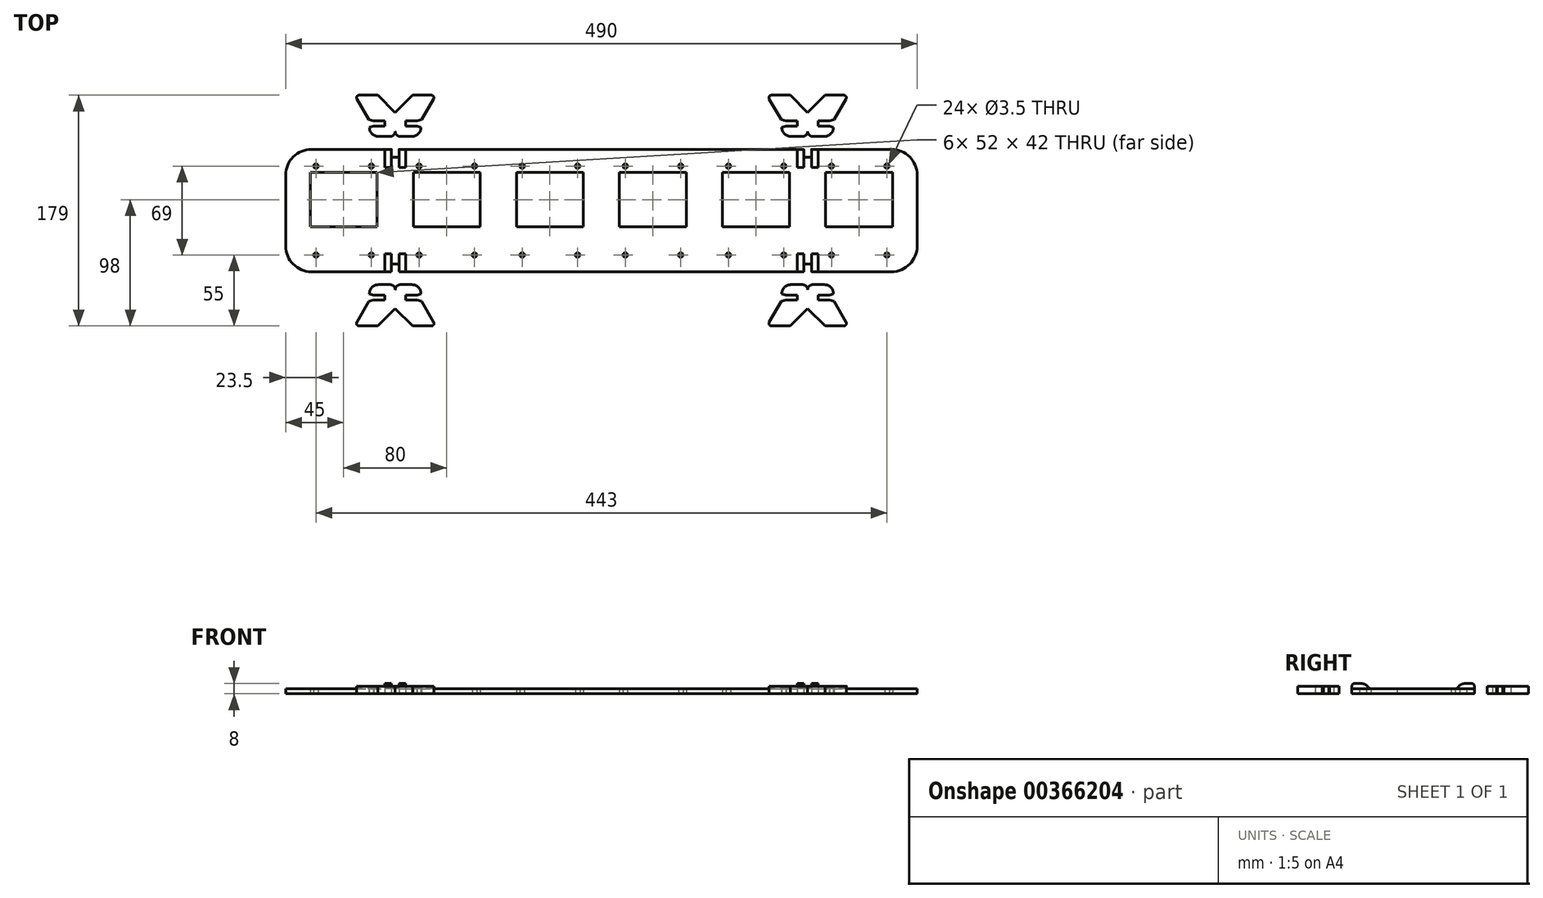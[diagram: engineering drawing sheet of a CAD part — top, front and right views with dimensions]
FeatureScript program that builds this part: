
annotation { "Feature Type Name" : "Feature", "Feature Type Description" : "" }
export const myFeature = defineFeature(function(context is Context, id is Id, definition is map)
    precondition{}
    {
        {
            var Q0;
            Q0=qCreatedBy(makeId("Top.planeOp"),FACE);
            var sketch = newSketch(context, id + "F0", { "sketchPlane" : qUnion([Q0])});
            skLineSegment(sketch, "E0.bottom", {"start": v(-245, -47.5) * mm, "end": v(245, -47.5) * mm});
            skLineSegment(sketch, "E0.top", {"start": v(-245, 47.5) * mm, "end": v(245, 47.5) * mm});
            skLineSegment(sketch, "E0.left", {"start": v(-245, -47.5) * mm, "end": v(-245, 47.5) * mm});
            skLineSegment(sketch, "E0.right", {"start": v(245, -47.5) * mm, "end": v(245, 47.5) * mm});
            skPoint(sketch, "E0.middle", {"position": v(0, 0) * mm});
            skLineSegment(sketch, "E1", {"start": v(-245, 0) * mm, "end": v(245, 0) * mm, "construction": true});
            skLineSegment(sketch, "E2.bottom", {"start": v(-175, -37.5) * mm, "end": v(-225, -37.5) * mm, "construction": true});
            skLineSegment(sketch, "E2.top", {"start": v(-175, 37.5) * mm, "end": v(-225, 37.5) * mm, "construction": true});
            skLineSegment(sketch, "E2.left", {"start": v(-175, -37.5) * mm, "end": v(-175, 37.5) * mm, "construction": true});
            skLineSegment(sketch, "E2.right", {"start": v(-225, -37.5) * mm, "end": v(-225, 37.5) * mm, "construction": true});
            skPoint(sketch, "E2.middle", {"position": v(-200, 0) * mm});
            skLineSegment(sketch, "E3.bottom", {"start": v(-95, -37.5) * mm, "end": v(-145, -37.5) * mm, "construction": true});
            skLineSegment(sketch, "E3.top", {"start": v(-95, 37.5) * mm, "end": v(-145, 37.5) * mm, "construction": true});
            skLineSegment(sketch, "E3.left", {"start": v(-95, -37.5) * mm, "end": v(-95, 37.5) * mm, "construction": true});
            skLineSegment(sketch, "E3.right", {"start": v(-145, -37.5) * mm, "end": v(-145, 37.5) * mm, "construction": true});
            skPoint(sketch, "E3.middle", {"position": v(-120, 0) * mm});
            skLineSegment(sketch, "E4.bottom", {"start": v(-15, -37.5) * mm, "end": v(-65, -37.5) * mm, "construction": true});
            skLineSegment(sketch, "E4.top", {"start": v(-15, 37.5) * mm, "end": v(-65, 37.5) * mm, "construction": true});
            skLineSegment(sketch, "E4.left", {"start": v(-15, -37.5) * mm, "end": v(-15, 37.5) * mm, "construction": true});
            skLineSegment(sketch, "E4.right", {"start": v(-65, -37.5) * mm, "end": v(-65, 37.5) * mm, "construction": true});
            skPoint(sketch, "E4.middle", {"position": v(-40, 0) * mm});
            skLineSegment(sketch, "E5.bottom", {"start": v(65, -37.5) * mm, "end": v(15, -37.5) * mm, "construction": true});
            skLineSegment(sketch, "E5.top", {"start": v(65, 37.5) * mm, "end": v(15, 37.5) * mm, "construction": true});
            skLineSegment(sketch, "E5.left", {"start": v(65, -37.5) * mm, "end": v(65, 37.5) * mm, "construction": true});
            skLineSegment(sketch, "E5.right", {"start": v(15, -37.5) * mm, "end": v(15, 37.5) * mm, "construction": true});
            skPoint(sketch, "E5.middle", {"position": v(40, 0) * mm});
            skLineSegment(sketch, "E6.bottom", {"start": v(145, -37.5) * mm, "end": v(95, -37.5) * mm, "construction": true});
            skLineSegment(sketch, "E6.top", {"start": v(145, 37.5) * mm, "end": v(95, 37.5) * mm, "construction": true});
            skLineSegment(sketch, "E6.left", {"start": v(145, -37.5) * mm, "end": v(145, 37.5) * mm, "construction": true});
            skLineSegment(sketch, "E6.right", {"start": v(95, -37.5) * mm, "end": v(95, 37.5) * mm, "construction": true});
            skPoint(sketch, "E6.middle", {"position": v(120, 0) * mm});
            skLineSegment(sketch, "E7.bottom", {"start": v(225, -37.5) * mm, "end": v(175, -37.5) * mm, "construction": true});
            skLineSegment(sketch, "E7.top", {"start": v(225, 37.5) * mm, "end": v(175, 37.5) * mm, "construction": true});
            skLineSegment(sketch, "E7.left", {"start": v(225, -37.5) * mm, "end": v(225, 37.5) * mm, "construction": true});
            skLineSegment(sketch, "E7.right", {"start": v(175, -37.5) * mm, "end": v(175, 37.5) * mm, "construction": true});
            skPoint(sketch, "E7.middle", {"position": v(200, 0) * mm});
            skLineSegment(sketch, "E8.bottom", {"start": v(305, -37.5) * mm, "end": v(255, -37.5) * mm, "construction": true});
            skLineSegment(sketch, "E8.top", {"start": v(305, 37.5) * mm, "end": v(255, 37.5) * mm, "construction": true});
            skLineSegment(sketch, "E8.left", {"start": v(305, -37.5) * mm, "end": v(305, 37.5) * mm, "construction": true});
            skLineSegment(sketch, "E8.right", {"start": v(255, -37.5) * mm, "end": v(255, 37.5) * mm, "construction": true});
            skPoint(sketch, "E8.middle", {"position": v(280, 0) * mm});
            skLineSegment(sketch, "E9.bottom", {"start": v(385, -37.5) * mm, "end": v(335, -37.5) * mm, "construction": true});
            skLineSegment(sketch, "E9.top", {"start": v(385, 37.5) * mm, "end": v(335, 37.5) * mm, "construction": true});
            skLineSegment(sketch, "E9.left", {"start": v(385, -37.5) * mm, "end": v(385, 37.5) * mm, "construction": true});
            skLineSegment(sketch, "E9.right", {"start": v(335, -37.5) * mm, "end": v(335, 37.5) * mm, "construction": true});
            skPoint(sketch, "E9.middle", {"position": v(360, 0) * mm});
            skLineSegment(sketch, "E10", {"start": v(-225, 0) * mm, "end": v(-245, 0) * mm, "construction": true});
            skLineSegment(sketch, "E11", {"start": v(335, 37.5) * mm, "end": v(325, 37.5) * mm});
            skLineSegment(sketch, "E12", {"start": v(315, 37.5) * mm, "end": v(325, 37.5) * mm});
            skLineSegment(sketch, "E13", {"start": v(315, 37.5) * mm, "end": v(305, 37.5) * mm, "construction": true});
            skLineSegment(sketch, "E14", {"start": v(255, 37.5) * mm, "end": v(245, 37.5) * mm, "construction": true});
            skLineSegment(sketch, "E15", {"start": v(245, 37.5) * mm, "end": v(235, 37.5) * mm, "construction": true});
            skLineSegment(sketch, "E16", {"start": v(235, 37.5) * mm, "end": v(225, 37.5) * mm, "construction": true});
            skLineSegment(sketch, "E17", {"start": v(155, 37.5) * mm, "end": v(145, 37.5) * mm, "construction": true});
            skLineSegment(sketch, "E18", {"start": v(95, 37.5) * mm, "end": v(85, 37.5) * mm, "construction": true});
            skLineSegment(sketch, "E19", {"start": v(85, 37.5) * mm, "end": v(75, 37.5) * mm, "construction": true});
            skLineSegment(sketch, "E20", {"start": v(75, 37.5) * mm, "end": v(65, 37.5) * mm, "construction": true});
            skLineSegment(sketch, "E21", {"start": v(15, 37.5) * mm, "end": v(5, 37.5) * mm, "construction": true});
            skLineSegment(sketch, "E22", {"start": v(5, 37.5) * mm, "end": v(-5, 37.5) * mm, "construction": true});
            skLineSegment(sketch, "E23", {"start": v(-5, 37.5) * mm, "end": v(-15, 37.5) * mm, "construction": true});
            skLineSegment(sketch, "E24", {"start": v(-65, 37.5) * mm, "end": v(-75, 37.5) * mm, "construction": true});
            skLineSegment(sketch, "E25", {"start": v(-75, 37.5) * mm, "end": v(-85, 37.5) * mm, "construction": true});
            skLineSegment(sketch, "E26", {"start": v(-85, 37.5) * mm, "end": v(-95, 37.5) * mm, "construction": true});
            skLineSegment(sketch, "E27", {"start": v(-145, 37.5) * mm, "end": v(-155, 37.5) * mm, "construction": true});
            skLineSegment(sketch, "E28", {"start": v(-155, 37.5) * mm, "end": v(-165, 37.5) * mm, "construction": true});
            skLineSegment(sketch, "E29", {"start": v(-165, 37.5) * mm, "end": v(-175, 37.5) * mm, "construction": true});
            skLineSegment(sketch, "E30", {"start": v(155, 37.5) * mm, "end": v(165, 37.5) * mm, "construction": true});
            skLineSegment(sketch, "E31", {"start": v(165, 37.5) * mm, "end": v(175, 37.5) * mm, "construction": true});
            skLineSegment(sketch, "E32", {"start": v(385, 37.5) * mm, "end": v(395, 37.5) * mm, "construction": true});
            skLineSegment(sketch, "E33.bottom", {"start": v(465, 37.5) * mm, "end": v(415, 37.5) * mm, "construction": true});
            skLineSegment(sketch, "E33.top", {"start": v(465, -37.5) * mm, "end": v(415, -37.5) * mm, "construction": true});
            skLineSegment(sketch, "E33.left", {"start": v(465, 37.5) * mm, "end": v(465, -37.5) * mm, "construction": true});
            skLineSegment(sketch, "E33.right", {"start": v(415, 37.5) * mm, "end": v(415, -37.5) * mm, "construction": true});
            skPoint(sketch, "E33.middle", {"position": v(440, 0) * mm});
            skLineSegment(sketch, "E34", {"start": v(395, 37.5) * mm, "end": v(405, 37.5) * mm, "construction": true});
            skLineSegment(sketch, "E35", {"start": v(405, 37.5) * mm, "end": v(415, 37.5) * mm, "construction": true});
            skLineSegment(sketch, "E36", {"start": v(465, 37.5) * mm, "end": v(475, 37.5) * mm, "construction": true});
            skLineSegment(sketch, "E37", {"start": v(475, 37.5) * mm, "end": v(485, 37.5) * mm, "construction": true});
            skLineSegment(sketch, "E38", {"start": v(485, 37.5) * mm, "end": v(495, 37.5) * mm, "construction": true});
            skLineSegment(sketch, "E39.bottom", {"start": v(495, 37.5) * mm, "end": v(545, 37.5) * mm, "construction": true});
            skLineSegment(sketch, "E39.top", {"start": v(495, -37.5) * mm, "end": v(545, -37.5) * mm, "construction": true});
            skLineSegment(sketch, "E39.left", {"start": v(495, 37.5) * mm, "end": v(495, -37.5) * mm, "construction": true});
            skLineSegment(sketch, "E39.right", {"start": v(545, 37.5) * mm, "end": v(545, -37.5) * mm, "construction": true});
            skPoint(sketch, "E39.middle", {"position": v(520, 0) * mm});
            skLineSegment(sketch, "E40.bottom", {"start": v(-178.5, -34.5) * mm, "end": v(-221.5, -34.5) * mm, "construction": true});
            skLineSegment(sketch, "E40.top", {"start": v(-178.5, 34.5) * mm, "end": v(-221.5, 34.5) * mm, "construction": true});
            skLineSegment(sketch, "E40.left", {"start": v(-178.5, -34.5) * mm, "end": v(-178.5, 34.5) * mm, "construction": true});
            skLineSegment(sketch, "E40.right", {"start": v(-221.5, -34.5) * mm, "end": v(-221.5, 34.5) * mm, "construction": true});
            skCircle(sketch, "E41", {"center": v(-178.5, 34.5) * mm, "radius": 1.75 * mm});
            skCircle(sketch, "E42", {"center": v(-221.5, 34.5) * mm, "radius": 1.75 * mm});
            skCircle(sketch, "E43", {"center": v(-221.5, -34.5) * mm, "radius": 1.75 * mm});
            skCircle(sketch, "E44", {"center": v(-178.5, -34.5) * mm, "radius": 1.75 * mm});
            skLineSegment(sketch, "E45.bottom", {"start": v(-174, -12.5) * mm, "end": v(-226, -12.5) * mm});
            skLineSegment(sketch, "E45.top", {"start": v(-174, 29.5) * mm, "end": v(-226, 29.5) * mm});
            skLineSegment(sketch, "E45.left", {"start": v(-174, -12.5) * mm, "end": v(-174, 29.5) * mm});
            skLineSegment(sketch, "E45.right", {"start": v(-226, -12.5) * mm, "end": v(-226, 29.5) * mm});
            skPoint(sketch, "E45.middle", {"position": v(-200, 8.5) * mm});
            skLineSegment(sketch, "E46.bottom", {"start": v(-98.5, -34.5) * mm, "end": v(-141.5, -34.5) * mm, "construction": true});
            skLineSegment(sketch, "E46.top", {"start": v(-98.5, 34.5) * mm, "end": v(-141.5, 34.5) * mm, "construction": true});
            skLineSegment(sketch, "E46.left", {"start": v(-98.5, -34.5) * mm, "end": v(-98.5, 34.5) * mm, "construction": true});
            skLineSegment(sketch, "E46.right", {"start": v(-141.5, -34.5) * mm, "end": v(-141.5, 34.5) * mm, "construction": true});
            skCircle(sketch, "E47", {"center": v(-98.5, 34.5) * mm, "radius": 1.75 * mm});
            skCircle(sketch, "E48", {"center": v(-141.5, 34.5) * mm, "radius": 1.75 * mm});
            skCircle(sketch, "E49", {"center": v(-141.5, -34.5) * mm, "radius": 1.75 * mm});
            skCircle(sketch, "E50", {"center": v(-98.5, -34.5) * mm, "radius": 1.75 * mm});
            skLineSegment(sketch, "E51.bottom", {"start": v(-94, -12.5) * mm, "end": v(-146, -12.5) * mm});
            skLineSegment(sketch, "E51.top", {"start": v(-94, 29.5) * mm, "end": v(-146, 29.5) * mm});
            skLineSegment(sketch, "E51.left", {"start": v(-94, -12.5) * mm, "end": v(-94, 29.5) * mm});
            skLineSegment(sketch, "E51.right", {"start": v(-146, -12.5) * mm, "end": v(-146, 29.5) * mm});
            skPoint(sketch, "E51.middle", {"position": v(-120, 8.5) * mm});
            skLineSegment(sketch, "E52.bottom", {"start": v(-18.5, -34.5) * mm, "end": v(-61.5, -34.5) * mm, "construction": true});
            skLineSegment(sketch, "E52.top", {"start": v(-18.5, 34.5) * mm, "end": v(-61.5, 34.5) * mm, "construction": true});
            skLineSegment(sketch, "E52.left", {"start": v(-18.5, -34.5) * mm, "end": v(-18.5, 34.5) * mm, "construction": true});
            skLineSegment(sketch, "E52.right", {"start": v(-61.5, -34.5) * mm, "end": v(-61.5, 34.5) * mm, "construction": true});
            skCircle(sketch, "E53", {"center": v(-18.5, 34.5) * mm, "radius": 1.75 * mm});
            skCircle(sketch, "E54", {"center": v(-61.5, 34.5) * mm, "radius": 1.75 * mm});
            skCircle(sketch, "E55", {"center": v(-61.5, -34.5) * mm, "radius": 1.75 * mm});
            skCircle(sketch, "E56", {"center": v(-18.5, -34.5) * mm, "radius": 1.75 * mm});
            skLineSegment(sketch, "E57.bottom", {"start": v(-14, -12.5) * mm, "end": v(-66, -12.5) * mm});
            skLineSegment(sketch, "E57.top", {"start": v(-14, 29.5) * mm, "end": v(-66, 29.5) * mm});
            skLineSegment(sketch, "E57.left", {"start": v(-14, -12.5) * mm, "end": v(-14, 29.5) * mm});
            skLineSegment(sketch, "E57.right", {"start": v(-66, -12.5) * mm, "end": v(-66, 29.5) * mm});
            skPoint(sketch, "E57.middle", {"position": v(-40, 8.5) * mm});
            skLineSegment(sketch, "E58.bottom", {"start": v(61.5, -34.5) * mm, "end": v(18.5, -34.5) * mm, "construction": true});
            skLineSegment(sketch, "E58.top", {"start": v(61.5, 34.5) * mm, "end": v(18.5, 34.5) * mm, "construction": true});
            skLineSegment(sketch, "E58.left", {"start": v(61.5, -34.5) * mm, "end": v(61.5, 34.5) * mm, "construction": true});
            skLineSegment(sketch, "E58.right", {"start": v(18.5, -34.5) * mm, "end": v(18.5, 34.5) * mm, "construction": true});
            skCircle(sketch, "E59", {"center": v(61.5, 34.5) * mm, "radius": 1.75 * mm});
            skCircle(sketch, "E60", {"center": v(18.5, 34.5) * mm, "radius": 1.75 * mm});
            skCircle(sketch, "E61", {"center": v(18.5, -34.5) * mm, "radius": 1.75 * mm});
            skCircle(sketch, "E62", {"center": v(61.5, -34.5) * mm, "radius": 1.75 * mm});
            skLineSegment(sketch, "E63.bottom", {"start": v(66, -12.5) * mm, "end": v(14, -12.5) * mm});
            skLineSegment(sketch, "E63.top", {"start": v(66, 29.5) * mm, "end": v(14, 29.5) * mm});
            skLineSegment(sketch, "E63.left", {"start": v(66, -12.5) * mm, "end": v(66, 29.5) * mm});
            skLineSegment(sketch, "E63.right", {"start": v(14, -12.5) * mm, "end": v(14, 29.5) * mm});
            skPoint(sketch, "E63.middle", {"position": v(40, 8.5) * mm});
            skLineSegment(sketch, "E64.bottom", {"start": v(141.5, -34.5) * mm, "end": v(98.5, -34.5) * mm, "construction": true});
            skLineSegment(sketch, "E64.top", {"start": v(141.5, 34.5) * mm, "end": v(98.5, 34.5) * mm, "construction": true});
            skLineSegment(sketch, "E64.left", {"start": v(141.5, -34.5) * mm, "end": v(141.5, 34.5) * mm, "construction": true});
            skLineSegment(sketch, "E64.right", {"start": v(98.5, -34.5) * mm, "end": v(98.5, 34.5) * mm, "construction": true});
            skCircle(sketch, "E65", {"center": v(141.5, 34.5) * mm, "radius": 1.75 * mm});
            skCircle(sketch, "E66", {"center": v(98.5, 34.5) * mm, "radius": 1.75 * mm});
            skCircle(sketch, "E67", {"center": v(98.5, -34.5) * mm, "radius": 1.75 * mm});
            skCircle(sketch, "E68", {"center": v(141.5, -34.5) * mm, "radius": 1.75 * mm});
            skLineSegment(sketch, "E69.bottom", {"start": v(146, -12.5) * mm, "end": v(94, -12.5) * mm});
            skLineSegment(sketch, "E69.top", {"start": v(146, 29.5) * mm, "end": v(94, 29.5) * mm});
            skLineSegment(sketch, "E69.left", {"start": v(146, -12.5) * mm, "end": v(146, 29.5) * mm});
            skLineSegment(sketch, "E69.right", {"start": v(94, -12.5) * mm, "end": v(94, 29.5) * mm});
            skPoint(sketch, "E69.middle", {"position": v(120, 8.5) * mm});
            skLineSegment(sketch, "E70.bottom", {"start": v(221.5, -34.5) * mm, "end": v(178.5, -34.5) * mm, "construction": true});
            skLineSegment(sketch, "E70.top", {"start": v(221.5, 34.5) * mm, "end": v(178.5, 34.5) * mm, "construction": true});
            skLineSegment(sketch, "E70.left", {"start": v(221.5, -34.5) * mm, "end": v(221.5, 34.5) * mm, "construction": true});
            skLineSegment(sketch, "E70.right", {"start": v(178.5, -34.5) * mm, "end": v(178.5, 34.5) * mm, "construction": true});
            skCircle(sketch, "E71", {"center": v(221.5, 34.5) * mm, "radius": 1.75 * mm});
            skCircle(sketch, "E72", {"center": v(178.5, 34.5) * mm, "radius": 1.75 * mm});
            skCircle(sketch, "E73", {"center": v(178.5, -34.5) * mm, "radius": 1.75 * mm});
            skCircle(sketch, "E74", {"center": v(221.5, -34.5) * mm, "radius": 1.75 * mm});
            skLineSegment(sketch, "E75.bottom", {"start": v(226, -12.5) * mm, "end": v(174, -12.5) * mm});
            skLineSegment(sketch, "E75.top", {"start": v(226, 29.5) * mm, "end": v(174, 29.5) * mm});
            skLineSegment(sketch, "E75.left", {"start": v(226, -12.5) * mm, "end": v(226, 29.5) * mm});
            skLineSegment(sketch, "E75.right", {"start": v(174, -12.5) * mm, "end": v(174, 29.5) * mm});
            skPoint(sketch, "E75.middle", {"position": v(200, 8.5) * mm});
            skLineSegment(sketch, "E76.bottom", {"start": v(301.5, -34.5) * mm, "end": v(258.5, -34.5) * mm, "construction": true});
            skLineSegment(sketch, "E76.top", {"start": v(301.5, 34.5) * mm, "end": v(258.5, 34.5) * mm, "construction": true});
            skLineSegment(sketch, "E76.left", {"start": v(301.5, -34.5) * mm, "end": v(301.5, 34.5) * mm, "construction": true});
            skLineSegment(sketch, "E76.right", {"start": v(258.5, -34.5) * mm, "end": v(258.5, 34.5) * mm, "construction": true});
            skCircle(sketch, "E77", {"center": v(301.5, 34.5) * mm, "radius": 1.75 * mm});
            skCircle(sketch, "E78", {"center": v(258.5, 34.5) * mm, "radius": 1.75 * mm});
            skCircle(sketch, "E79", {"center": v(258.5, -34.5) * mm, "radius": 1.75 * mm});
            skCircle(sketch, "E80", {"center": v(301.5, -34.5) * mm, "radius": 1.75 * mm});
            skLineSegment(sketch, "E81.bottom", {"start": v(306, -12.5) * mm, "end": v(254, -12.5) * mm});
            skLineSegment(sketch, "E81.top", {"start": v(306, 29.5) * mm, "end": v(254, 29.5) * mm});
            skLineSegment(sketch, "E81.left", {"start": v(306, -12.5) * mm, "end": v(306, 29.5) * mm});
            skLineSegment(sketch, "E81.right", {"start": v(254, -12.5) * mm, "end": v(254, 29.5) * mm});
            skPoint(sketch, "E81.middle", {"position": v(280, 8.5) * mm});
            skLineSegment(sketch, "E82.bottom", {"start": v(381.5, -34.5) * mm, "end": v(338.5, -34.5) * mm, "construction": true});
            skLineSegment(sketch, "E82.top", {"start": v(381.5, 34.5) * mm, "end": v(338.5, 34.5) * mm, "construction": true});
            skLineSegment(sketch, "E82.left", {"start": v(381.5, -34.5) * mm, "end": v(381.5, 34.5) * mm, "construction": true});
            skLineSegment(sketch, "E82.right", {"start": v(338.5, -34.5) * mm, "end": v(338.5, 34.5) * mm, "construction": true});
            skCircle(sketch, "E83", {"center": v(381.5, 34.5) * mm, "radius": 1.75 * mm});
            skCircle(sketch, "E84", {"center": v(338.5, 34.5) * mm, "radius": 1.75 * mm});
            skCircle(sketch, "E85", {"center": v(338.5, -34.5) * mm, "radius": 1.75 * mm});
            skCircle(sketch, "E86", {"center": v(381.5, -34.5) * mm, "radius": 1.75 * mm});
            skLineSegment(sketch, "E87.bottom", {"start": v(386, -12.5) * mm, "end": v(334, -12.5) * mm});
            skLineSegment(sketch, "E87.top", {"start": v(386, 29.5) * mm, "end": v(334, 29.5) * mm});
            skLineSegment(sketch, "E87.left", {"start": v(386, -12.5) * mm, "end": v(386, 29.5) * mm});
            skLineSegment(sketch, "E87.right", {"start": v(334, -12.5) * mm, "end": v(334, 29.5) * mm});
            skPoint(sketch, "E87.middle", {"position": v(360, 8.5) * mm});
            skLineSegment(sketch, "E88.bottom", {"start": v(461.5, -34.5) * mm, "end": v(418.5, -34.5) * mm, "construction": true});
            skLineSegment(sketch, "E88.top", {"start": v(461.5, 34.5) * mm, "end": v(418.5, 34.5) * mm, "construction": true});
            skLineSegment(sketch, "E88.left", {"start": v(461.5, -34.5) * mm, "end": v(461.5, 34.5) * mm, "construction": true});
            skLineSegment(sketch, "E88.right", {"start": v(418.5, -34.5) * mm, "end": v(418.5, 34.5) * mm, "construction": true});
            skCircle(sketch, "E89", {"center": v(461.5, 34.5) * mm, "radius": 1.75 * mm});
            skCircle(sketch, "E90", {"center": v(418.5, 34.5) * mm, "radius": 1.75 * mm});
            skCircle(sketch, "E91", {"center": v(418.5, -34.5) * mm, "radius": 1.75 * mm});
            skCircle(sketch, "E92", {"center": v(461.5, -34.5) * mm, "radius": 1.75 * mm});
            skLineSegment(sketch, "E93.bottom", {"start": v(466, -12.5) * mm, "end": v(414, -12.5) * mm});
            skLineSegment(sketch, "E93.top", {"start": v(466, 29.5) * mm, "end": v(414, 29.5) * mm});
            skLineSegment(sketch, "E93.left", {"start": v(466, -12.5) * mm, "end": v(466, 29.5) * mm});
            skLineSegment(sketch, "E93.right", {"start": v(414, -12.5) * mm, "end": v(414, 29.5) * mm});
            skPoint(sketch, "E93.middle", {"position": v(440, 8.5) * mm});
            skLineSegment(sketch, "E94.bottom", {"start": v(541.5, -34.5) * mm, "end": v(498.5, -34.5) * mm, "construction": true});
            skLineSegment(sketch, "E94.top", {"start": v(541.5, 34.5) * mm, "end": v(498.5, 34.5) * mm, "construction": true});
            skLineSegment(sketch, "E94.left", {"start": v(541.5, -34.5) * mm, "end": v(541.5, 34.5) * mm, "construction": true});
            skLineSegment(sketch, "E94.right", {"start": v(498.5, -34.5) * mm, "end": v(498.5, 34.5) * mm, "construction": true});
            skCircle(sketch, "E95", {"center": v(541.5, 34.5) * mm, "radius": 1.75 * mm});
            skCircle(sketch, "E96", {"center": v(498.5, 34.5) * mm, "radius": 1.75 * mm});
            skCircle(sketch, "E97", {"center": v(498.5, -34.5) * mm, "radius": 1.75 * mm});
            skCircle(sketch, "E98", {"center": v(541.5, -34.5) * mm, "radius": 1.75 * mm});
            skLineSegment(sketch, "E99.bottom", {"start": v(546, -12.5) * mm, "end": v(494, -12.5) * mm});
            skLineSegment(sketch, "E99.top", {"start": v(546, 29.5) * mm, "end": v(494, 29.5) * mm});
            skLineSegment(sketch, "E99.left", {"start": v(546, -12.5) * mm, "end": v(546, 29.5) * mm});
            skLineSegment(sketch, "E99.right", {"start": v(494, -12.5) * mm, "end": v(494, 29.5) * mm});
            skPoint(sketch, "E99.middle", {"position": v(520, 8.5) * mm});
            skLineSegment(sketch, "E100", {"start": v(545, 37.5) * mm, "end": v(555, 37.5) * mm, "construction": true});
            skLineSegment(sketch, "E101.bottom", {"start": v(-157, -47.5) * mm, "end": v(-163, -47.5) * mm});
            skLineSegment(sketch, "E101.top", {"start": v(-157, -41.5) * mm, "end": v(-163, -41.5) * mm});
            skLineSegment(sketch, "E101.left", {"start": v(-157, -47.5) * mm, "end": v(-157, -41.5) * mm});
            skLineSegment(sketch, "E101.right", {"start": v(-163, -47.5) * mm, "end": v(-163, -41.5) * mm});
            skPoint(sketch, "E101.middle", {"position": v(-160, -44.5) * mm});
            skLineSegment(sketch, "E102.bottom", {"start": v(163, -41.5) * mm, "end": v(157, -41.5) * mm});
            skLineSegment(sketch, "E102.top", {"start": v(163, -47.5) * mm, "end": v(157, -47.5) * mm});
            skLineSegment(sketch, "E102.left", {"start": v(163, -41.5) * mm, "end": v(163, -47.5) * mm});
            skLineSegment(sketch, "E102.right", {"start": v(157, -41.5) * mm, "end": v(157, -47.5) * mm});
            skPoint(sketch, "E102.middle", {"position": v(160, -44.5) * mm});
            skLineSegment(sketch, "E103.bottom", {"start": v(-157, 47.5) * mm, "end": v(-163, 47.5) * mm});
            skLineSegment(sketch, "E103.top", {"start": v(-157, 41.5) * mm, "end": v(-163, 41.5) * mm});
            skLineSegment(sketch, "E103.left", {"start": v(-157, 47.5) * mm, "end": v(-157, 41.5) * mm});
            skLineSegment(sketch, "E103.right", {"start": v(-163, 47.5) * mm, "end": v(-163, 41.5) * mm});
            skPoint(sketch, "E103.middle", {"position": v(-160, 44.5) * mm});
            skLineSegment(sketch, "E104.bottom", {"start": v(163, 47.5) * mm, "end": v(157, 47.5) * mm});
            skLineSegment(sketch, "E104.top", {"start": v(163, 41.5) * mm, "end": v(157, 41.5) * mm});
            skLineSegment(sketch, "E104.left", {"start": v(163, 47.5) * mm, "end": v(163, 41.5) * mm});
            skLineSegment(sketch, "E104.right", {"start": v(157, 47.5) * mm, "end": v(157, 41.5) * mm});
            skPoint(sketch, "E104.middle", {"position": v(160, 44.5) * mm});
            skSolve(sketch);
        }
        {
            var Q0;
            Q0=makeQuery(id+"F0.imprint","IMPRINT",FACE,{"disambiguationData":[TD([[makeQuery(id+"F0.imprint","IMPRINT",EDGE,{"derivedFrom":sQuery(id+"F0.wireOp",EDGE,"E0.bottom")}),1.0]])]});
            extrude(context, id + "F1", {"entities" : qUnion([Q0]), "depth" : 4 * mm});
        }
        {
            var Q0;
            Q0=makeQuery(id+"F1.opExtrude","SWEPT_EDGE",EDGE,{"disambiguationData":[OSD([sQuery(id+"F0.wireOp",EDGE,"E0.bottom"),sQuery(id+"F0.wireOp",EDGE,"E0.left")])]});
            var Q1;
            Q1=makeQuery(id+"F1.opExtrude","SWEPT_EDGE",EDGE,{"disambiguationData":[OSD([sQuery(id+"F0.wireOp",EDGE,"E0.top"),sQuery(id+"F0.wireOp",EDGE,"E0.left")])]});
            var Q2;
            Q2=makeQuery(id+"F1.opExtrude","SWEPT_EDGE",EDGE,{"disambiguationData":[OSD([sQuery(id+"F0.wireOp",EDGE,"E0.top"),sQuery(id+"F0.wireOp",EDGE,"E0.right")])]});
            var Q3;
            Q3=makeQuery(id+"F1.opExtrude","SWEPT_EDGE",EDGE,{"disambiguationData":[OSD([sQuery(id+"F0.wireOp",EDGE,"E0.bottom"),sQuery(id+"F0.wireOp",EDGE,"E0.right")])]});
            fillet(context, id + "F2", {"entities" : qUnion([Q0, Q1, Q2, Q3]), "radius" : 20 * mm, "tangentPropagation" : true, "allowEdgeOverflow" : false});
        }
        {
            var Q0;
            Q0=qCreatedBy(makeId("Top.planeOp"),FACE);
            var sketch = newSketch(context, id + "F3", { "sketchPlane" : qUnion([Q0])});
            skLineSegment(sketch, "E105.bottom", {"start": v(-152, -65.5) * mm, "end": v(-140, -65.5) * mm});
            skLineSegment(sketch, "E105.top", {"start": v(-152, -69.5) * mm, "end": v(-140, -69.5) * mm});
            skLineSegment(sketch, "E105.left", {"start": v(-152, -65.5) * mm, "end": v(-152, -69.5) * mm});
            skLineSegment(sketch, "E105.right", {"start": v(-140, -65.5) * mm, "end": v(-140, -69.5) * mm, "construction": true});
            skLineSegment(sketch, "E106", {"start": v(-160, -61.5) * mm, "end": v(-160, -75.95) * mm});
            skLineSegment(sketch, "E107", {"start": v(-160, -75.95) * mm, "end": v(-146.45, -89.5) * mm});
            skLineSegment(sketch, "E108", {"start": v(-146.45, -89.5) * mm, "end": v(-131.92, -89.5) * mm});
            skLineSegment(sketch, "E109", {"start": v(-130.19, -86.5) * mm, "end": v(-140, -69.5) * mm});
            skLineSegment(sketch, "E110", {"start": v(-156, -57.5) * mm, "end": v(-147, -57.5) * mm});
            skLineSegment(sketch, "E111", {"start": v(-140, -65.5) * mm, "end": v(-140, -64.5) * mm});
            skPoint(sketch, "E112.visualSharp", {"position": v(-140, -57.5) * mm});
            skArc(sketch, "E112.filletArc", {"start": v(-140, -64.5) * mm, "mid": v(-142.05, -59.55) * mm, "end": v(-147, -57.5) * mm});
            skPoint(sketch, "E113.visualSharp", {"position": v(-160, -57.5) * mm});
            skArc(sketch, "E113.filletArc", {"start": v(-156, -57.5) * mm, "mid": v(-158.83, -58.67) * mm, "end": v(-160, -61.5) * mm});
            skPoint(sketch, "E114.visualSharp", {"position": v(-128.45, -89.5) * mm});
            skArc(sketch, "E114.filletArc", {"start": v(-131.92, -89.5) * mm, "mid": v(-130.19, -88.5) * mm, "end": v(-130.19, -86.5) * mm});
            skLineSegment(sketch, "E115", {"start": v(-143, -69.5) * mm, "end": v(-139.45, -70.45) * mm});
            skLineSegment(sketch, "E116", {"start": v(-143, -65.5) * mm, "end": v(-140, -64.7) * mm});
            skLineSegment(sketch, "E117.MirrorCS", {"start": v(-180, -65.5) * mm, "end": v(-180, -64.5) * mm});
            skLineSegment(sketch, "E118.MirrorCS", {"start": v(-180, -65.5) * mm, "end": v(-180, -69.5) * mm, "construction": true});
            skLineSegment(sketch, "E119.MirrorCS", {"start": v(-177, -69.5) * mm, "end": v(-180.55, -70.45) * mm});
            skLineSegment(sketch, "E120.MirrorCS", {"start": v(-177, -65.5) * mm, "end": v(-180, -64.7) * mm});
            skLineSegment(sketch, "E121.MirrorCS", {"start": v(-168, -65.5) * mm, "end": v(-168, -69.5) * mm});
            skArc(sketch, "E122.MirrorCS", {"start": v(-188.08, -89.5) * mm, "mid": v(-189.81, -88.5) * mm, "end": v(-189.81, -86.5) * mm});
            skLineSegment(sketch, "E123.MirrorCS", {"start": v(-168, -65.5) * mm, "end": v(-180, -65.5) * mm});
            skArc(sketch, "E124.MirrorCS", {"start": v(-164, -57.5) * mm, "mid": v(-161.17, -58.67) * mm, "end": v(-160, -61.5) * mm});
            skPoint(sketch, "E125.MirrorP", {"position": v(-191.55, -89.5) * mm});
            skLineSegment(sketch, "E126.MirrorCS", {"start": v(-173.55, -89.5) * mm, "end": v(-188.08, -89.5) * mm});
            skLineSegment(sketch, "E127.MirrorCS", {"start": v(-160, -75.95) * mm, "end": v(-173.55, -89.5) * mm});
            skPoint(sketch, "E128.MirrorP", {"position": v(-180, -57.5) * mm});
            skLineSegment(sketch, "E129.MirrorCS", {"start": v(-168, -69.5) * mm, "end": v(-180, -69.5) * mm});
            skLineSegment(sketch, "E130.MirrorCS", {"start": v(-164, -57.5) * mm, "end": v(-173, -57.5) * mm});
            skLineSegment(sketch, "E131.MirrorCS", {"start": v(-189.81, -86.5) * mm, "end": v(-180, -69.5) * mm});
            skArc(sketch, "E132.MirrorCS", {"start": v(-180, -64.5) * mm, "mid": v(-177.95, -59.55) * mm, "end": v(-173, -57.5) * mm});
            skLineSegment(sketch, "E133.0", {"start": v(-157, -41.5) * mm, "end": v(-163, -41.5) * mm});
            skPoint(sketch, "E134", {"position": v(-160, -41.5) * mm});
            skSolve(sketch);
        }
        {
            var Q0;
            Q0=makeQuery(id+"F3.imprint","IMPRINT",FACE,{"disambiguationData":[TD([[makeQuery(id+"F3.imprint","IMPRINT",EDGE,{"derivedFrom":sQuery(id+"F3.wireOp",EDGE,"E106")}),-1.0]])]});
            var Q1;
            {var subQ6=sQuery(id+"F3.wireOp",EDGE,"E105.left");Q1=makeQuery(id+"F3.imprint","IMPRINT",FACE,{"disambiguationData":[TD([[makeQuery(id+"F3.imprint","IMPRINT",EDGE,{"derivedFrom":subQ6}),-1.0]])]});}
            extrude(context, id + "F4", {"entities" : qUnion([Q0, Q1]), "depth" : 6 * mm});
        }
        {
            var Q0;
            Q0=makeQuery(id+"F1.opExtrude","CAP_FACE",FACE,{"disambiguationData":[OSD([sQuery(id+"F0.wireOp",EDGE,"E0.bottom"),sQuery(id+"F0.wireOp",EDGE,"E0.top"),sQuery(id+"F0.wireOp",EDGE,"E0.left"),sQuery(id+"F0.wireOp",EDGE,"E0.right"),sQuery(id+"F0.wireOp",EDGE,"E41"),sQuery(id+"F0.wireOp",EDGE,"E42"),sQuery(id+"F0.wireOp",EDGE,"E43"),sQuery(id+"F0.wireOp",EDGE,"E44"),sQuery(id+"F0.wireOp",EDGE,"E45.bottom"),sQuery(id+"F0.wireOp",EDGE,"E45.top"),sQuery(id+"F0.wireOp",EDGE,"E45.left"),sQuery(id+"F0.wireOp",EDGE,"E45.right"),sQuery(id+"F0.wireOp",EDGE,"E47"),sQuery(id+"F0.wireOp",EDGE,"E48"),sQuery(id+"F0.wireOp",EDGE,"E49"),sQuery(id+"F0.wireOp",EDGE,"E50"),sQuery(id+"F0.wireOp",EDGE,"E51.bottom"),sQuery(id+"F0.wireOp",EDGE,"E51.top"),sQuery(id+"F0.wireOp",EDGE,"E51.left"),sQuery(id+"F0.wireOp",EDGE,"E51.right"),sQuery(id+"F0.wireOp",EDGE,"E53"),sQuery(id+"F0.wireOp",EDGE,"E54"),sQuery(id+"F0.wireOp",EDGE,"E55"),sQuery(id+"F0.wireOp",EDGE,"E56"),sQuery(id+"F0.wireOp",EDGE,"E57.bottom"),sQuery(id+"F0.wireOp",EDGE,"E57.top"),sQuery(id+"F0.wireOp",EDGE,"E57.left"),sQuery(id+"F0.wireOp",EDGE,"E57.right"),sQuery(id+"F0.wireOp",EDGE,"E59"),sQuery(id+"F0.wireOp",EDGE,"E60"),sQuery(id+"F0.wireOp",EDGE,"E61"),sQuery(id+"F0.wireOp",EDGE,"E62"),sQuery(id+"F0.wireOp",EDGE,"E63.bottom"),sQuery(id+"F0.wireOp",EDGE,"E63.top"),sQuery(id+"F0.wireOp",EDGE,"E63.left"),sQuery(id+"F0.wireOp",EDGE,"E63.right"),sQuery(id+"F0.wireOp",EDGE,"E65"),sQuery(id+"F0.wireOp",EDGE,"E66"),sQuery(id+"F0.wireOp",EDGE,"E67"),sQuery(id+"F0.wireOp",EDGE,"E68"),sQuery(id+"F0.wireOp",EDGE,"E69.bottom"),sQuery(id+"F0.wireOp",EDGE,"E69.top"),sQuery(id+"F0.wireOp",EDGE,"E69.left"),sQuery(id+"F0.wireOp",EDGE,"E69.right"),sQuery(id+"F0.wireOp",EDGE,"E71"),sQuery(id+"F0.wireOp",EDGE,"E72"),sQuery(id+"F0.wireOp",EDGE,"E73"),sQuery(id+"F0.wireOp",EDGE,"E74"),sQuery(id+"F0.wireOp",EDGE,"E75.bottom"),sQuery(id+"F0.wireOp",EDGE,"E75.top"),sQuery(id+"F0.wireOp",EDGE,"E75.left"),sQuery(id+"F0.wireOp",EDGE,"E75.right"),sQuery(id+"F0.wireOp",EDGE,"E101.top"),sQuery(id+"F0.wireOp",EDGE,"E101.left"),sQuery(id+"F0.wireOp",EDGE,"E101.right"),sQuery(id+"F0.wireOp",EDGE,"E102.bottom"),sQuery(id+"F0.wireOp",EDGE,"E102.left"),sQuery(id+"F0.wireOp",EDGE,"E102.right"),sQuery(id+"F0.wireOp",EDGE,"E103.top"),sQuery(id+"F0.wireOp",EDGE,"E103.left"),sQuery(id+"F0.wireOp",EDGE,"E103.right"),sQuery(id+"F0.wireOp",EDGE,"E104.top"),sQuery(id+"F0.wireOp",EDGE,"E104.left"),sQuery(id+"F0.wireOp",EDGE,"E104.right")])],"isStart":false});
            var sketch = newSketch(context, id + "F5", { "sketchPlane" : qUnion([Q0])});
            skLineSegment(sketch, "E135.bottom", {"start": v(-163, -47.5) * mm, "end": v(-168, -47.5) * mm});
            skLineSegment(sketch, "E135.top", {"start": v(-163, -33.5) * mm, "end": v(-168, -33.5) * mm});
            skLineSegment(sketch, "E135.left", {"start": v(-163, -47.5) * mm, "end": v(-163, -33.5) * mm});
            skLineSegment(sketch, "E135.right", {"start": v(-168, -47.5) * mm, "end": v(-168, -33.5) * mm});
            skLineSegment(sketch, "E136.bottom", {"start": v(-157, -47.5) * mm, "end": v(-152, -47.5) * mm});
            skLineSegment(sketch, "E136.top", {"start": v(-157, -33.5) * mm, "end": v(-152, -33.5) * mm});
            skLineSegment(sketch, "E136.left", {"start": v(-157, -47.5) * mm, "end": v(-157, -33.5) * mm});
            skLineSegment(sketch, "E136.right", {"start": v(-152, -47.5) * mm, "end": v(-152, -33.5) * mm});
            skLineSegment(sketch, "E137.bottom", {"start": v(-163, 47.5) * mm, "end": v(-168, 47.5) * mm});
            skLineSegment(sketch, "E137.top", {"start": v(-163, 33.5) * mm, "end": v(-168, 33.5) * mm});
            skLineSegment(sketch, "E137.left", {"start": v(-163, 47.5) * mm, "end": v(-163, 33.5) * mm});
            skLineSegment(sketch, "E137.right", {"start": v(-168, 47.5) * mm, "end": v(-168, 33.5) * mm});
            skLineSegment(sketch, "E138.bottom", {"start": v(-157, 47.5) * mm, "end": v(-152, 47.5) * mm});
            skLineSegment(sketch, "E138.top", {"start": v(-157, 33.5) * mm, "end": v(-152, 33.5) * mm});
            skLineSegment(sketch, "E138.left", {"start": v(-157, 47.5) * mm, "end": v(-157, 33.5) * mm});
            skLineSegment(sketch, "E138.right", {"start": v(-152, 47.5) * mm, "end": v(-152, 33.5) * mm});
            skLineSegment(sketch, "E139.bottom", {"start": v(157, 47.5) * mm, "end": v(152, 47.5) * mm});
            skLineSegment(sketch, "E139.top", {"start": v(157, 33.5) * mm, "end": v(152, 33.5) * mm});
            skLineSegment(sketch, "E139.left", {"start": v(157, 47.5) * mm, "end": v(157, 33.5) * mm});
            skLineSegment(sketch, "E139.right", {"start": v(152, 47.5) * mm, "end": v(152, 33.5) * mm});
            skLineSegment(sketch, "E140.bottom", {"start": v(163, 47.5) * mm, "end": v(168, 47.5) * mm});
            skLineSegment(sketch, "E140.top", {"start": v(163, 33.5) * mm, "end": v(168, 33.5) * mm});
            skLineSegment(sketch, "E140.left", {"start": v(163, 47.5) * mm, "end": v(163, 33.5) * mm});
            skLineSegment(sketch, "E140.right", {"start": v(168, 47.5) * mm, "end": v(168, 33.5) * mm});
            skLineSegment(sketch, "E141.bottom", {"start": v(157, -47.5) * mm, "end": v(152, -47.5) * mm});
            skLineSegment(sketch, "E141.top", {"start": v(157, -33.5) * mm, "end": v(152, -33.5) * mm});
            skLineSegment(sketch, "E141.left", {"start": v(157, -47.5) * mm, "end": v(157, -33.5) * mm});
            skLineSegment(sketch, "E141.right", {"start": v(152, -47.5) * mm, "end": v(152, -33.5) * mm});
            skLineSegment(sketch, "E142.bottom", {"start": v(163, -47.5) * mm, "end": v(168, -47.5) * mm});
            skLineSegment(sketch, "E142.top", {"start": v(163, -33.5) * mm, "end": v(168, -33.5) * mm});
            skLineSegment(sketch, "E142.left", {"start": v(163, -47.5) * mm, "end": v(163, -33.5) * mm});
            skLineSegment(sketch, "E142.right", {"start": v(168, -47.5) * mm, "end": v(168, -33.5) * mm});
            skSolve(sketch);
        }
        {
            var Q0;
            {var subQ3=sQuery(id+"F5.wireOp",EDGE,"E135.bottom");Q0=makeQuery(id+"F5.imprint","IMPRINT",FACE,{"disambiguationData":[TD([[makeQuery(id+"F5.imprint","IMPRINT",EDGE,{"derivedFrom":subQ3}),1.0]])]});}
            var Q1;
            {var subQ3=sQuery(id+"F5.wireOp",EDGE,"E136.bottom");Q1=makeQuery(id+"F5.imprint","IMPRINT",FACE,{"disambiguationData":[TD([[makeQuery(id+"F5.imprint","IMPRINT",EDGE,{"derivedFrom":subQ3}),1.0]])]});}
            var Q2;
            {var subQ1=sQuery(id+"F5.wireOp",EDGE,"E137.bottom");Q2=makeQuery(id+"F5.imprint","IMPRINT",FACE,{"disambiguationData":[TD([[makeQuery(id+"F5.imprint","IMPRINT",EDGE,{"derivedFrom":subQ1}),-1.0]])]});}
            var Q3;
            {var subQ1=sQuery(id+"F5.wireOp",EDGE,"E138.bottom");Q3=makeQuery(id+"F5.imprint","IMPRINT",FACE,{"disambiguationData":[TD([[makeQuery(id+"F5.imprint","IMPRINT",EDGE,{"derivedFrom":subQ1}),-1.0]])]});}
            var Q4;
            {var subQ3=sQuery(id+"F5.wireOp",EDGE,"E142.bottom");Q4=makeQuery(id+"F5.imprint","IMPRINT",FACE,{"disambiguationData":[TD([[makeQuery(id+"F5.imprint","IMPRINT",EDGE,{"derivedFrom":subQ3}),1.0]])]});}
            var Q5;
            {var subQ3=sQuery(id+"F5.wireOp",EDGE,"E141.bottom");Q5=makeQuery(id+"F5.imprint","IMPRINT",FACE,{"disambiguationData":[TD([[makeQuery(id+"F5.imprint","IMPRINT",EDGE,{"derivedFrom":subQ3}),1.0]])]});}
            var Q6;
            {var subQ1=sQuery(id+"F5.wireOp",EDGE,"E139.bottom");Q6=makeQuery(id+"F5.imprint","IMPRINT",FACE,{"disambiguationData":[TD([[makeQuery(id+"F5.imprint","IMPRINT",EDGE,{"derivedFrom":subQ1}),-1.0]])]});}
            var Q7;
            {var subQ3=sQuery(id+"F5.wireOp",EDGE,"E140.bottom");Q7=makeQuery(id+"F5.imprint","IMPRINT",FACE,{"disambiguationData":[TD([[makeQuery(id+"F5.imprint","IMPRINT",EDGE,{"derivedFrom":subQ3}),-1.0]])]});}
            extrude(context, id + "F6", {"entities" : qUnion([Q0, Q1, Q2, Q3, Q4, Q5, Q6, Q7]), "operationType" : NewBodyOperationType.ADD, "depth" : 4 * mm});
        }
        {
            var Q0;
            Q0=makeQuery(id+"F6.opExtrude","CAP_EDGE",EDGE,{"disambiguationData":[OSD([sQuery(id+"F5.wireOp",EDGE,"E135.top")])],"isStart":false});
            var Q1;
            Q1=makeQuery(id+"F6.opExtrude","CAP_EDGE",EDGE,{"disambiguationData":[OSD([sQuery(id+"F5.wireOp",EDGE,"E136.top")])],"isStart":false});
            var Q2;
            Q2=makeQuery(id+"F6.opExtrude","CAP_EDGE",EDGE,{"disambiguationData":[OSD([sQuery(id+"F5.wireOp",EDGE,"E137.top")])],"isStart":false});
            var Q3;
            Q3=makeQuery(id+"F6.opExtrude","CAP_EDGE",EDGE,{"disambiguationData":[OSD([sQuery(id+"F5.wireOp",EDGE,"E138.top")])],"isStart":false});
            var Q4;
            Q4=makeQuery(id+"F6.opExtrude","CAP_EDGE",EDGE,{"disambiguationData":[OSD([sQuery(id+"F5.wireOp",EDGE,"E139.top")])],"isStart":false});
            var Q5;
            Q5=makeQuery(id+"F6.opExtrude","CAP_EDGE",EDGE,{"disambiguationData":[OSD([sQuery(id+"F5.wireOp",EDGE,"E140.top")])],"isStart":false});
            var Q6;
            Q6=makeQuery(id+"F6.opExtrude","CAP_EDGE",EDGE,{"disambiguationData":[OSD([sQuery(id+"F5.wireOp",EDGE,"E142.top")])],"isStart":false});
            var Q7;
            Q7=makeQuery(id+"F6.opExtrude","CAP_EDGE",EDGE,{"disambiguationData":[OSD([sQuery(id+"F5.wireOp",EDGE,"E141.top")])],"isStart":false});
            chamfer(context, id + "F7", {"entities" : qUnion([Q0, Q1, Q2, Q3, Q4, Q5, Q6, Q7]), "width" : 4 * mm, "tangentPropagation" : true});
        }
        {
            var Q0;
            {var subQ0=sQuery(id+"F5.wireOp",EDGE,"E137.top");Q0=makeQuery(id+"F7.opChamfer","BLEND_EDGE",EDGE,{"blendedFrom":[makeQuery(id+"F6.opExtrude","CAP_EDGE",EDGE,{"disambiguationData":[OSD([subQ0])],"isStart":false}),makeQuery(id+"F6.opExtrude","CAP_FACE",FACE,{"disambiguationData":[OSD([sQuery(id+"F5.wireOp",EDGE,"E137.bottom"),subQ0,sQuery(id+"F5.wireOp",EDGE,"E137.left"),sQuery(id+"F5.wireOp",EDGE,"E137.right")])],"isStart":false})],"blendedInto":[makeQuery(id+"F6.opExtrude","CAP_FACE",FACE,{"disambiguationData":[OSD([sQuery(id+"F5.wireOp",EDGE,"E137.bottom"),subQ0,sQuery(id+"F5.wireOp",EDGE,"E137.left"),sQuery(id+"F5.wireOp",EDGE,"E137.right")])],"isStart":false})]});}
            var Q1;
            {var subQ0=sQuery(id+"F5.wireOp",EDGE,"E138.top");Q1=makeQuery(id+"F7.opChamfer","BLEND_EDGE",EDGE,{"blendedFrom":[makeQuery(id+"F6.opExtrude","CAP_EDGE",EDGE,{"disambiguationData":[OSD([subQ0])],"isStart":false}),makeQuery(id+"F6.opExtrude","CAP_FACE",FACE,{"disambiguationData":[OSD([sQuery(id+"F5.wireOp",EDGE,"E138.bottom"),subQ0,sQuery(id+"F5.wireOp",EDGE,"E138.left"),sQuery(id+"F5.wireOp",EDGE,"E138.right")])],"isStart":false})],"blendedInto":[makeQuery(id+"F6.opExtrude","CAP_FACE",FACE,{"disambiguationData":[OSD([sQuery(id+"F5.wireOp",EDGE,"E138.bottom"),subQ0,sQuery(id+"F5.wireOp",EDGE,"E138.left"),sQuery(id+"F5.wireOp",EDGE,"E138.right")])],"isStart":false})]});}
            var Q2;
            {var subQ0=sQuery(id+"F5.wireOp",EDGE,"E135.top");Q2=makeQuery(id+"F7.opChamfer","BLEND_EDGE",EDGE,{"blendedFrom":[makeQuery(id+"F6.opExtrude","CAP_EDGE",EDGE,{"disambiguationData":[OSD([subQ0])],"isStart":false}),makeQuery(id+"F6.opExtrude","CAP_FACE",FACE,{"disambiguationData":[OSD([sQuery(id+"F5.wireOp",EDGE,"E135.bottom"),subQ0,sQuery(id+"F5.wireOp",EDGE,"E135.left"),sQuery(id+"F5.wireOp",EDGE,"E135.right")])],"isStart":false})],"blendedInto":[makeQuery(id+"F6.opExtrude","CAP_FACE",FACE,{"disambiguationData":[OSD([sQuery(id+"F5.wireOp",EDGE,"E135.bottom"),subQ0,sQuery(id+"F5.wireOp",EDGE,"E135.left"),sQuery(id+"F5.wireOp",EDGE,"E135.right")])],"isStart":false})]});}
            var Q3;
            {var subQ0=sQuery(id+"F5.wireOp",EDGE,"E136.top");Q3=makeQuery(id+"F7.opChamfer","BLEND_EDGE",EDGE,{"blendedFrom":[makeQuery(id+"F6.opExtrude","CAP_EDGE",EDGE,{"disambiguationData":[OSD([subQ0])],"isStart":false}),makeQuery(id+"F6.opExtrude","CAP_FACE",FACE,{"disambiguationData":[OSD([sQuery(id+"F5.wireOp",EDGE,"E136.bottom"),subQ0,sQuery(id+"F5.wireOp",EDGE,"E136.left"),sQuery(id+"F5.wireOp",EDGE,"E136.right")])],"isStart":false})],"blendedInto":[makeQuery(id+"F6.opExtrude","CAP_FACE",FACE,{"disambiguationData":[OSD([sQuery(id+"F5.wireOp",EDGE,"E136.bottom"),subQ0,sQuery(id+"F5.wireOp",EDGE,"E136.left"),sQuery(id+"F5.wireOp",EDGE,"E136.right")])],"isStart":false})]});}
            var Q4;
            {var subQ0=sQuery(id+"F5.wireOp",EDGE,"E142.top");Q4=makeQuery(id+"F7.opChamfer","BLEND_EDGE",EDGE,{"blendedFrom":[makeQuery(id+"F6.opExtrude","CAP_EDGE",EDGE,{"disambiguationData":[OSD([subQ0])],"isStart":false}),makeQuery(id+"F6.opExtrude","CAP_FACE",FACE,{"disambiguationData":[OSD([sQuery(id+"F5.wireOp",EDGE,"E142.bottom"),subQ0,sQuery(id+"F5.wireOp",EDGE,"E142.left"),sQuery(id+"F5.wireOp",EDGE,"E142.right")])],"isStart":false})],"blendedInto":[makeQuery(id+"F6.opExtrude","CAP_FACE",FACE,{"disambiguationData":[OSD([sQuery(id+"F5.wireOp",EDGE,"E142.bottom"),subQ0,sQuery(id+"F5.wireOp",EDGE,"E142.left"),sQuery(id+"F5.wireOp",EDGE,"E142.right")])],"isStart":false})]});}
            var Q5;
            {var subQ0=sQuery(id+"F5.wireOp",EDGE,"E141.top");Q5=makeQuery(id+"F7.opChamfer","BLEND_EDGE",EDGE,{"blendedFrom":[makeQuery(id+"F6.opExtrude","CAP_EDGE",EDGE,{"disambiguationData":[OSD([subQ0])],"isStart":false}),makeQuery(id+"F6.opExtrude","CAP_FACE",FACE,{"disambiguationData":[OSD([sQuery(id+"F5.wireOp",EDGE,"E141.bottom"),subQ0,sQuery(id+"F5.wireOp",EDGE,"E141.left"),sQuery(id+"F5.wireOp",EDGE,"E141.right")])],"isStart":false})],"blendedInto":[makeQuery(id+"F6.opExtrude","CAP_FACE",FACE,{"disambiguationData":[OSD([sQuery(id+"F5.wireOp",EDGE,"E141.bottom"),subQ0,sQuery(id+"F5.wireOp",EDGE,"E141.left"),sQuery(id+"F5.wireOp",EDGE,"E141.right")])],"isStart":false})]});}
            var Q6;
            {var subQ0=sQuery(id+"F5.wireOp",EDGE,"E139.top");Q6=makeQuery(id+"F7.opChamfer","BLEND_EDGE",EDGE,{"blendedFrom":[makeQuery(id+"F6.opExtrude","CAP_EDGE",EDGE,{"disambiguationData":[OSD([subQ0])],"isStart":false}),makeQuery(id+"F6.opExtrude","CAP_FACE",FACE,{"disambiguationData":[OSD([sQuery(id+"F5.wireOp",EDGE,"E139.bottom"),subQ0,sQuery(id+"F5.wireOp",EDGE,"E139.left"),sQuery(id+"F5.wireOp",EDGE,"E139.right")])],"isStart":false})],"blendedInto":[makeQuery(id+"F6.opExtrude","CAP_FACE",FACE,{"disambiguationData":[OSD([sQuery(id+"F5.wireOp",EDGE,"E139.bottom"),subQ0,sQuery(id+"F5.wireOp",EDGE,"E139.left"),sQuery(id+"F5.wireOp",EDGE,"E139.right")])],"isStart":false})]});}
            var Q7;
            {var subQ0=sQuery(id+"F5.wireOp",EDGE,"E140.top");Q7=makeQuery(id+"F7.opChamfer","BLEND_EDGE",EDGE,{"blendedFrom":[makeQuery(id+"F6.opExtrude","CAP_EDGE",EDGE,{"disambiguationData":[OSD([subQ0])],"isStart":false}),makeQuery(id+"F6.opExtrude","CAP_FACE",FACE,{"disambiguationData":[OSD([sQuery(id+"F5.wireOp",EDGE,"E140.bottom"),subQ0,sQuery(id+"F5.wireOp",EDGE,"E140.left"),sQuery(id+"F5.wireOp",EDGE,"E140.right")])],"isStart":false})],"blendedInto":[makeQuery(id+"F6.opExtrude","CAP_FACE",FACE,{"disambiguationData":[OSD([sQuery(id+"F5.wireOp",EDGE,"E140.bottom"),subQ0,sQuery(id+"F5.wireOp",EDGE,"E140.left"),sQuery(id+"F5.wireOp",EDGE,"E140.right")])],"isStart":false})]});}
            fillet(context, id + "F8", {"entities" : qUnion([Q0, Q1, Q2, Q3, Q4, Q5, Q6, Q7]), "radius" : 7 * mm, "tangentPropagation" : true, "allowEdgeOverflow" : false});
        }
        {
            var Q0;
            Q0=makeQuery(id+"F6.opExtrude","CAP_EDGE",EDGE,{"disambiguationData":[OSD([sQuery(id+"F5.wireOp",EDGE,"E135.bottom")])],"isStart":false});
            var Q1;
            Q1=makeQuery(id+"F6.opExtrude","CAP_EDGE",EDGE,{"disambiguationData":[OSD([sQuery(id+"F5.wireOp",EDGE,"E136.bottom")])],"isStart":false});
            var Q2;
            Q2=makeQuery(id+"F6.opExtrude","CAP_EDGE",EDGE,{"disambiguationData":[OSD([sQuery(id+"F5.wireOp",EDGE,"E137.bottom")])],"isStart":false});
            var Q3;
            Q3=makeQuery(id+"F6.opExtrude","CAP_EDGE",EDGE,{"disambiguationData":[OSD([sQuery(id+"F5.wireOp",EDGE,"E138.bottom")])],"isStart":false});
            var Q4;
            Q4=makeQuery(id+"F6.opExtrude","CAP_EDGE",EDGE,{"disambiguationData":[OSD([sQuery(id+"F5.wireOp",EDGE,"E142.bottom")])],"isStart":false});
            var Q5;
            Q5=makeQuery(id+"F6.opExtrude","CAP_EDGE",EDGE,{"disambiguationData":[OSD([sQuery(id+"F5.wireOp",EDGE,"E141.bottom")])],"isStart":false});
            var Q6;
            Q6=makeQuery(id+"F6.opExtrude","CAP_EDGE",EDGE,{"disambiguationData":[OSD([sQuery(id+"F5.wireOp",EDGE,"E139.bottom")])],"isStart":false});
            var Q7;
            Q7=makeQuery(id+"F6.opExtrude","CAP_EDGE",EDGE,{"disambiguationData":[OSD([sQuery(id+"F5.wireOp",EDGE,"E140.bottom")])],"isStart":false});
            fillet(context, id + "F9", {"entities" : qUnion([Q0, Q1, Q2, Q3, Q4, Q5, Q6, Q7]), "radius" : 2 * mm, "tangentPropagation" : true, "allowEdgeOverflow" : false});
        }
        {
            var Q0;
            Q0=makeQuery(id+"F4.opExtrude","SWEPT_BODY",BODY,{"disambiguationData":[OSD([sQuery(id+"F3.wireOp",EDGE,"E105.bottom"),sQuery(id+"F3.wireOp",EDGE,"E105.top"),sQuery(id+"F3.wireOp",EDGE,"E105.left"),sQuery(id+"F3.wireOp",EDGE,"E107"),sQuery(id+"F3.wireOp",EDGE,"E108"),sQuery(id+"F3.wireOp",EDGE,"E109"),sQuery(id+"F3.wireOp",EDGE,"E110"),sQuery(id+"F3.wireOp",EDGE,"E111"),sQuery(id+"F3.wireOp",EDGE,"E112.filletArc"),sQuery(id+"F3.wireOp",EDGE,"E113.filletArc"),sQuery(id+"F3.wireOp",EDGE,"E114.filletArc"),sQuery(id+"F3.wireOp",EDGE,"E115"),sQuery(id+"F3.wireOp",EDGE,"E116"),sQuery(id+"F3.wireOp",EDGE,"E117.MirrorCS"),sQuery(id+"F3.wireOp",EDGE,"E119.MirrorCS"),sQuery(id+"F3.wireOp",EDGE,"E120.MirrorCS"),sQuery(id+"F3.wireOp",EDGE,"E121.MirrorCS"),sQuery(id+"F3.wireOp",EDGE,"E122.MirrorCS"),sQuery(id+"F3.wireOp",EDGE,"E123.MirrorCS"),sQuery(id+"F3.wireOp",EDGE,"E124.MirrorCS"),sQuery(id+"F3.wireOp",EDGE,"E126.MirrorCS"),sQuery(id+"F3.wireOp",EDGE,"E127.MirrorCS"),sQuery(id+"F3.wireOp",EDGE,"E129.MirrorCS"),sQuery(id+"F3.wireOp",EDGE,"E130.MirrorCS"),sQuery(id+"F3.wireOp",EDGE,"E131.MirrorCS"),sQuery(id+"F3.wireOp",EDGE,"E132.MirrorCS")])]});
            var Q1;
            Q1=qCreatedBy(makeId("Right.planeOp"),FACE);
            mirror(context, id + "F10", {"entities" : qUnion([Q0]), "mirrorPlane" : qUnion([Q1])});
        }
        {
            var Q0;
            Q0=makeQuery(id+"F4.opExtrude","SWEPT_BODY",BODY,{"disambiguationData":[OSD([sQuery(id+"F3.wireOp",EDGE,"E105.bottom"),sQuery(id+"F3.wireOp",EDGE,"E105.top"),sQuery(id+"F3.wireOp",EDGE,"E105.left"),sQuery(id+"F3.wireOp",EDGE,"E107"),sQuery(id+"F3.wireOp",EDGE,"E108"),sQuery(id+"F3.wireOp",EDGE,"E109"),sQuery(id+"F3.wireOp",EDGE,"E110"),sQuery(id+"F3.wireOp",EDGE,"E111"),sQuery(id+"F3.wireOp",EDGE,"E112.filletArc"),sQuery(id+"F3.wireOp",EDGE,"E113.filletArc"),sQuery(id+"F3.wireOp",EDGE,"E114.filletArc"),sQuery(id+"F3.wireOp",EDGE,"E115"),sQuery(id+"F3.wireOp",EDGE,"E116"),sQuery(id+"F3.wireOp",EDGE,"E117.MirrorCS"),sQuery(id+"F3.wireOp",EDGE,"E119.MirrorCS"),sQuery(id+"F3.wireOp",EDGE,"E120.MirrorCS"),sQuery(id+"F3.wireOp",EDGE,"E121.MirrorCS"),sQuery(id+"F3.wireOp",EDGE,"E122.MirrorCS"),sQuery(id+"F3.wireOp",EDGE,"E123.MirrorCS"),sQuery(id+"F3.wireOp",EDGE,"E124.MirrorCS"),sQuery(id+"F3.wireOp",EDGE,"E126.MirrorCS"),sQuery(id+"F3.wireOp",EDGE,"E127.MirrorCS"),sQuery(id+"F3.wireOp",EDGE,"E129.MirrorCS"),sQuery(id+"F3.wireOp",EDGE,"E130.MirrorCS"),sQuery(id+"F3.wireOp",EDGE,"E131.MirrorCS"),sQuery(id+"F3.wireOp",EDGE,"E132.MirrorCS")])]});
            var Q1;
            Q1=makeQuery(id+"F10.opPattern","COPY",BODY,{"derivedFrom":makeQuery(id+"F4.opExtrude","SWEPT_BODY",BODY,{"disambiguationData":[OSD([sQuery(id+"F3.wireOp",EDGE,"E105.bottom"),sQuery(id+"F3.wireOp",EDGE,"E105.top"),sQuery(id+"F3.wireOp",EDGE,"E105.left"),sQuery(id+"F3.wireOp",EDGE,"E107"),sQuery(id+"F3.wireOp",EDGE,"E108"),sQuery(id+"F3.wireOp",EDGE,"E109"),sQuery(id+"F3.wireOp",EDGE,"E110"),sQuery(id+"F3.wireOp",EDGE,"E111"),sQuery(id+"F3.wireOp",EDGE,"E112.filletArc"),sQuery(id+"F3.wireOp",EDGE,"E113.filletArc"),sQuery(id+"F3.wireOp",EDGE,"E114.filletArc"),sQuery(id+"F3.wireOp",EDGE,"E115"),sQuery(id+"F3.wireOp",EDGE,"E116"),sQuery(id+"F3.wireOp",EDGE,"E117.MirrorCS"),sQuery(id+"F3.wireOp",EDGE,"E119.MirrorCS"),sQuery(id+"F3.wireOp",EDGE,"E120.MirrorCS"),sQuery(id+"F3.wireOp",EDGE,"E121.MirrorCS"),sQuery(id+"F3.wireOp",EDGE,"E122.MirrorCS"),sQuery(id+"F3.wireOp",EDGE,"E123.MirrorCS"),sQuery(id+"F3.wireOp",EDGE,"E124.MirrorCS"),sQuery(id+"F3.wireOp",EDGE,"E126.MirrorCS"),sQuery(id+"F3.wireOp",EDGE,"E127.MirrorCS"),sQuery(id+"F3.wireOp",EDGE,"E129.MirrorCS"),sQuery(id+"F3.wireOp",EDGE,"E130.MirrorCS"),sQuery(id+"F3.wireOp",EDGE,"E131.MirrorCS"),sQuery(id+"F3.wireOp",EDGE,"E132.MirrorCS")])]}),"instanceName":"1"});
            var Q2;
            Q2=qCreatedBy(makeId("Front.planeOp"),FACE);
            mirror(context, id + "F11", {"entities" : qUnion([Q0, Q1]), "mirrorPlane" : qUnion([Q2])});
        }
    });
